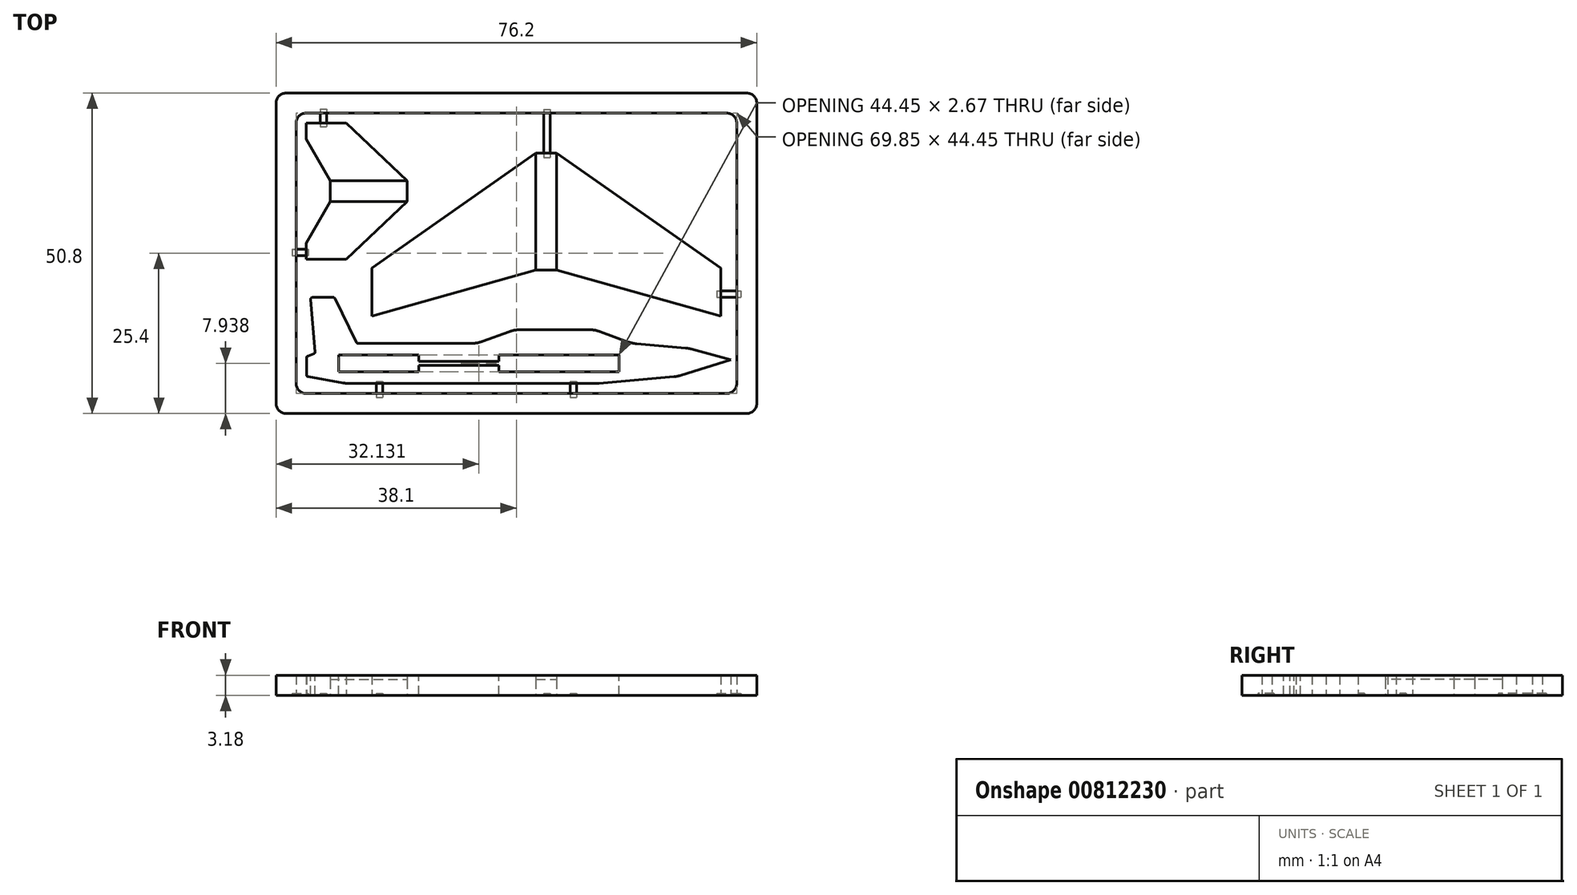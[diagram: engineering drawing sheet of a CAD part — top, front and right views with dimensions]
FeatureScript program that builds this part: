
annotation { "Feature Type Name" : "Feature", "Feature Type Description" : "" }
export const myFeature = defineFeature(function(context is Context, id is Id, definition is map)
    precondition{}
    {
        {
            var Q0;
            Q0=qCreatedBy(makeId("Top.planeOp"),FACE);
            var sketch = newSketch(context, id + "F0", { "sketchPlane" : qUnion([Q0])});
            skLineSegment(sketch, "E0.bottom", {"start": v(1.59, 0) * mm, "end": v(74.61, 0) * mm});
            skLineSegment(sketch, "E0.top", {"start": v(1.59, 50.8) * mm, "end": v(74.61, 50.8) * mm});
            skLineSegment(sketch, "E0.left", {"start": v(0, 1.59) * mm, "end": v(0, 49.21) * mm});
            skLineSegment(sketch, "E0.right", {"start": v(76.2, 1.59) * mm, "end": v(76.2, 49.21) * mm});
            skLineSegment(sketch, "E1.0", {"start": v(73.02, 4.76) * mm, "end": v(73.02, 46.04) * mm});
            skLineSegment(sketch, "E1.1", {"start": v(4.76, 3.17) * mm, "end": v(71.44, 3.17) * mm});
            skLineSegment(sketch, "E1.2", {"start": v(3.17, 4.76) * mm, "end": v(3.17, 46.04) * mm});
            skLineSegment(sketch, "E1.3", {"start": v(4.76, 47.63) * mm, "end": v(71.44, 47.63) * mm});
            skPoint(sketch, "E2.visualSharp", {"position": v(0, 50.8) * mm});
            skArc(sketch, "E2.filletArc", {"start": v(1.59, 50.8) * mm, "mid": v(0.46, 50.34) * mm, "end": v(0, 49.21) * mm});
            skPoint(sketch, "E3.visualSharp", {"position": v(76.2, 50.8) * mm});
            skArc(sketch, "E3.filletArc", {"start": v(76.2, 49.21) * mm, "mid": v(75.74, 50.34) * mm, "end": v(74.61, 50.8) * mm});
            skPoint(sketch, "E4.visualSharp", {"position": v(76.2, 0) * mm});
            skArc(sketch, "E4.filletArc", {"start": v(74.61, 0) * mm, "mid": v(75.74, 0.46) * mm, "end": v(76.2, 1.59) * mm});
            skPoint(sketch, "E5.visualSharp", {"position": v(0, 0) * mm});
            skArc(sketch, "E5.filletArc", {"start": v(0, 1.59) * mm, "mid": v(0.46, 0.46) * mm, "end": v(1.59, 0) * mm});
            skPoint(sketch, "E6.visualSharp", {"position": v(3.17, 3.17) * mm});
            skArc(sketch, "E6.filletArc", {"start": v(3.17, 4.76) * mm, "mid": v(3.64, 3.64) * mm, "end": v(4.76, 3.17) * mm});
            skPoint(sketch, "E7.visualSharp", {"position": v(3.17, 47.63) * mm});
            skArc(sketch, "E7.filletArc", {"start": v(4.76, 47.63) * mm, "mid": v(3.64, 47.16) * mm, "end": v(3.17, 46.04) * mm});
            skPoint(sketch, "E8.visualSharp", {"position": v(73.02, 47.63) * mm});
            skArc(sketch, "E8.filletArc", {"start": v(73.02, 46.04) * mm, "mid": v(72.56, 47.16) * mm, "end": v(71.44, 47.63) * mm});
            skPoint(sketch, "E9.visualSharp", {"position": v(73.02, 3.17) * mm});
            skArc(sketch, "E9.filletArc", {"start": v(71.44, 3.17) * mm, "mid": v(72.56, 3.64) * mm, "end": v(73.02, 4.76) * mm});
            skSolve(sketch);
        }
        {
            var Q0;
            Q0 = qSketchRegion(id + "F0", true);
            extrude(context, id + "F1", {"entities" : qUnion([Q0]), "depth" : 3.17 * mm, "offsetDistance" : 25.4 * mm});
        }
        {
            var Q0;
            Q0=qCreatedBy(makeId("Top.planeOp"),FACE);
            var sketch = newSketch(context, id + "F2", { "sketchPlane" : qUnion([Q0])});
            skLineSegment(sketch, "E10", {"start": v(11.08, 4.76) * mm, "end": v(50.96, 4.76) * mm});
            skLineSegment(sketch, "E11", {"start": v(50.96, 4.76) * mm, "end": v(63.6, 5.87) * mm});
            skLineSegment(sketch, "E12", {"start": v(56.49, 11.11) * mm, "end": v(50.52, 13.28) * mm});
            skLineSegment(sketch, "E13", {"start": v(12.8, 11.11) * mm, "end": v(9.25, 18.4) * mm});
            skLineSegment(sketch, "E14", {"start": v(9.25, 18.4) * mm, "end": v(5.44, 18.4) * mm});
            skLineSegment(sketch, "E15", {"start": v(50.52, 13.28) * mm, "end": v(37.82, 13.28) * mm});
            skLineSegment(sketch, "E16", {"start": v(37.82, 13.28) * mm, "end": v(31.85, 11.11) * mm});
            skLineSegment(sketch, "E17", {"start": v(31.85, 11.11) * mm, "end": v(12.8, 11.11) * mm});
            skLineSegment(sketch, "E18", {"start": v(11.08, 4.76) * mm, "end": v(4.83, 5.87) * mm});
            skLineSegment(sketch, "E19", {"start": v(4.83, 5.87) * mm, "end": v(4.83, 9.04) * mm});
            skLineSegment(sketch, "E20", {"start": v(4.83, 9.04) * mm, "end": v(6.21, 9.55) * mm});
            skLineSegment(sketch, "E21", {"start": v(6.21, 9.55) * mm, "end": v(5.44, 18.4) * mm});
            skLineSegment(sketch, "E22", {"start": v(56.49, 11.11) * mm, "end": v(65.34, 10.34) * mm});
            skLineSegment(sketch, "E23", {"start": v(65.34, 10.34) * mm, "end": v(72.1, 8.53) * mm});
            skLineSegment(sketch, "E24", {"start": v(72.1, 8.53) * mm, "end": v(63.6, 5.87) * mm});
            skSolve(sketch);
        }
        {
            var Q0;
            Q0 = qSketchRegion(id + "F2", true);
            extrude(context, id + "F3", {"entities" : qUnion([Q0]), "depth" : 3.17 * mm, "offsetDistance" : 25.4 * mm});
        }
        {
            var Q0;
            Q0=makeQuery(id+"F3.opExtrude","SWEPT_EDGE",EDGE,{"disambiguationData":[OSD([sQuery(id+"F2.wireOp",EDGE,"E22"),sQuery(id+"F2.wireOp",EDGE,"E23")])]});
            var Q1;
            Q1=makeQuery(id+"F3.opExtrude","SWEPT_EDGE",EDGE,{"disambiguationData":[OSD([sQuery(id+"F2.wireOp",EDGE,"E12"),sQuery(id+"F2.wireOp",EDGE,"E22")])]});
            var Q2;
            Q2=makeQuery(id+"F3.opExtrude","SWEPT_EDGE",EDGE,{"disambiguationData":[OSD([sQuery(id+"F2.wireOp",EDGE,"E12"),sQuery(id+"F2.wireOp",EDGE,"E15")])]});
            var Q3;
            Q3=makeQuery(id+"F3.opExtrude","SWEPT_EDGE",EDGE,{"disambiguationData":[OSD([sQuery(id+"F2.wireOp",EDGE,"E15"),sQuery(id+"F2.wireOp",EDGE,"E16")])]});
            var Q4;
            Q4=makeQuery(id+"F3.opExtrude","SWEPT_EDGE",EDGE,{"disambiguationData":[OSD([sQuery(id+"F2.wireOp",EDGE,"E16"),sQuery(id+"F2.wireOp",EDGE,"E17")])]});
            var Q5;
            Q5=makeQuery(id+"F3.opExtrude","SWEPT_EDGE",EDGE,{"disambiguationData":[OSD([sQuery(id+"F2.wireOp",EDGE,"E11"),sQuery(id+"F2.wireOp",EDGE,"E24")])]});
            var Q6;
            Q6=makeQuery(id+"F3.opExtrude","SWEPT_EDGE",EDGE,{"disambiguationData":[OSD([sQuery(id+"F2.wireOp",EDGE,"E10"),sQuery(id+"F2.wireOp",EDGE,"E11")])]});
            var Q7;
            Q7=makeQuery(id+"F3.opExtrude","SWEPT_EDGE",EDGE,{"disambiguationData":[OSD([sQuery(id+"F2.wireOp",EDGE,"E10"),sQuery(id+"F2.wireOp",EDGE,"E18")])]});
            fillet(context, id + "F4", {"entities" : qUnion([Q0, Q1, Q2, Q3, Q4, Q5, Q6, Q7]), "radius" : 5.08 * mm, "tangentPropagation" : true, "allowEdgeOverflow" : false});
        }
        {
            var Q0;
            Q0=makeQuery(id+"F3.opExtrude","SWEPT_EDGE",EDGE,{"disambiguationData":[OSD([sQuery(id+"F2.wireOp",EDGE,"E18"),sQuery(id+"F2.wireOp",EDGE,"E19")])]});
            var Q1;
            Q1=makeQuery(id+"F3.opExtrude","SWEPT_EDGE",EDGE,{"disambiguationData":[OSD([sQuery(id+"F2.wireOp",EDGE,"E19"),sQuery(id+"F2.wireOp",EDGE,"E20")])]});
            var Q2;
            Q2=makeQuery(id+"F3.opExtrude","SWEPT_EDGE",EDGE,{"disambiguationData":[OSD([sQuery(id+"F2.wireOp",EDGE,"E20"),sQuery(id+"F2.wireOp",EDGE,"E21")])]});
            var Q3;
            Q3=makeQuery(id+"F3.opExtrude","SWEPT_EDGE",EDGE,{"disambiguationData":[OSD([sQuery(id+"F2.wireOp",EDGE,"E14"),sQuery(id+"F2.wireOp",EDGE,"E21")])]});
            var Q4;
            Q4=makeQuery(id+"F3.opExtrude","SWEPT_EDGE",EDGE,{"disambiguationData":[OSD([sQuery(id+"F2.wireOp",EDGE,"E13"),sQuery(id+"F2.wireOp",EDGE,"E14")])]});
            var Q5;
            Q5=makeQuery(id+"F3.opExtrude","SWEPT_EDGE",EDGE,{"disambiguationData":[OSD([sQuery(id+"F2.wireOp",EDGE,"E13"),sQuery(id+"F2.wireOp",EDGE,"E17")])]});
            fillet(context, id + "F5", {"entities" : qUnion([Q0, Q1, Q2, Q3, Q4, Q5]), "radius" : 0.32 * mm, "tangentPropagation" : true, "allowEdgeOverflow" : false});
        }
        {
            var Q0;
            Q0=makeQuery(id+"F3.opExtrude","CAP_FACE",FACE,{"disambiguationData":[OSD([sQuery(id+"F2.wireOp",EDGE,"E10"),sQuery(id+"F2.wireOp",EDGE,"E11"),sQuery(id+"F2.wireOp",EDGE,"E12"),sQuery(id+"F2.wireOp",EDGE,"E13"),sQuery(id+"F2.wireOp",EDGE,"E14"),sQuery(id+"F2.wireOp",EDGE,"E15"),sQuery(id+"F2.wireOp",EDGE,"E16"),sQuery(id+"F2.wireOp",EDGE,"E17"),sQuery(id+"F2.wireOp",EDGE,"E18"),sQuery(id+"F2.wireOp",EDGE,"E19"),sQuery(id+"F2.wireOp",EDGE,"E20"),sQuery(id+"F2.wireOp",EDGE,"E21"),sQuery(id+"F2.wireOp",EDGE,"E22"),sQuery(id+"F2.wireOp",EDGE,"E23"),sQuery(id+"F2.wireOp",EDGE,"E24")])],"isStart":false});
            var sketch = newSketch(context, id + "F6", { "sketchPlane" : qUnion([Q0])});
            skLineSegment(sketch, "E25.bottom", {"start": v(9.9, 9.27) * mm, "end": v(22.6, 9.27) * mm});
            skLineSegment(sketch, "E25.top", {"start": v(9.9, 6.6) * mm, "end": v(22.6, 6.6) * mm});
            skLineSegment(sketch, "E25.left", {"start": v(9.9, 9.27) * mm, "end": v(9.9, 6.6) * mm});
            skLineSegment(sketch, "E25.right", {"start": v(22.6, 9.27) * mm, "end": v(22.6, 8.25) * mm});
            skLineSegment(sketch, "E26.bottom", {"start": v(35.3, 9.27) * mm, "end": v(54.36, 9.27) * mm});
            skLineSegment(sketch, "E26.top", {"start": v(35.3, 6.6) * mm, "end": v(54.36, 6.6) * mm});
            skLineSegment(sketch, "E26.left", {"start": v(35.3, 9.27) * mm, "end": v(35.3, 8.25) * mm});
            skLineSegment(sketch, "E26.right", {"start": v(54.36, 9.27) * mm, "end": v(54.36, 6.6) * mm});
            skLineSegment(sketch, "E27", {"start": v(22.6, 9.27) * mm, "end": v(22.6, 11.11) * mm, "construction": true});
            skLineSegment(sketch, "E28", {"start": v(22.6, 6.6) * mm, "end": v(22.6, 4.76) * mm, "construction": true});
            skLineSegment(sketch, "E29.bottom", {"start": v(22.6, 8.25) * mm, "end": v(35.3, 8.25) * mm});
            skLineSegment(sketch, "E29.top", {"start": v(22.6, 7.62) * mm, "end": v(35.3, 7.62) * mm});
            skLineSegment(sketch, "E30.trimOffspring", {"start": v(22.6, 7.62) * mm, "end": v(22.6, 6.6) * mm});
            skLineSegment(sketch, "E31.trimOffspring", {"start": v(35.3, 7.62) * mm, "end": v(35.3, 6.6) * mm});
            skSolve(sketch);
        }
        {
            var Q0;
            Q0 = qSketchRegion(id + "F6", true);
            extrude(context, id + "F7", {"entities" : qUnion([Q0]), "operationType" : NewBodyOperationType.REMOVE, "oppositeDirection" : true, "depth" : 25.4 * mm, "offsetDistance" : 25.4 * mm});
        }
        {
            var Q0;
            Q0=qCreatedBy(makeId("Top.planeOp"),FACE);
            var sketch = newSketch(context, id + "F8", { "sketchPlane" : qUnion([Q0])});
            skLineSegment(sketch, "E32.bottom", {"start": v(8.57, 36.9) * mm, "end": v(20.76, 36.9) * mm});
            skLineSegment(sketch, "E32.top", {"start": v(8.57, 33.6) * mm, "end": v(20.76, 33.6) * mm});
            skLineSegment(sketch, "E32.left", {"start": v(8.57, 36.9) * mm, "end": v(8.57, 33.6) * mm});
            skLineSegment(sketch, "E32.right", {"start": v(20.76, 36.9) * mm, "end": v(20.76, 33.6) * mm});
            skLineSegment(sketch, "E33", {"start": v(8.57, 36.9) * mm, "end": v(4.76, 43.5) * mm});
            skLineSegment(sketch, "E34", {"start": v(4.76, 43.5) * mm, "end": v(4.76, 46.04) * mm});
            skLineSegment(sketch, "E35", {"start": v(4.76, 46.04) * mm, "end": v(11.11, 46.04) * mm});
            skLineSegment(sketch, "E36", {"start": v(11.11, 46.04) * mm, "end": v(20.76, 36.9) * mm});
            skLineSegment(sketch, "E37", {"start": v(8.57, 33.6) * mm, "end": v(4.76, 27) * mm});
            skLineSegment(sketch, "E38", {"start": v(4.76, 27) * mm, "end": v(4.76, 24.46) * mm});
            skLineSegment(sketch, "E39", {"start": v(4.76, 24.46) * mm, "end": v(11.11, 24.46) * mm});
            skLineSegment(sketch, "E40", {"start": v(11.11, 24.46) * mm, "end": v(20.76, 33.6) * mm});
            skSolve(sketch);
        }
        {
            var Q0;
            Q0 = qSketchRegion(id + "F8", true);
            extrude(context, id + "F9", {"entities" : qUnion([Q0]), "depth" : 3.17 * mm, "offsetDistance" : 25.4 * mm});
        }
        {
            var Q0;
            Q0=makeQuery(id+"F9.opExtrude","CAP_FACE",FACE,{"disambiguationData":[OSD([sQuery(id+"F8.wireOp",EDGE,"E32.left"),sQuery(id+"F8.wireOp",EDGE,"E32.right"),sQuery(id+"F8.wireOp",EDGE,"E33"),sQuery(id+"F8.wireOp",EDGE,"E34"),sQuery(id+"F8.wireOp",EDGE,"E35"),sQuery(id+"F8.wireOp",EDGE,"E36"),sQuery(id+"F8.wireOp",EDGE,"E37"),sQuery(id+"F8.wireOp",EDGE,"E38"),sQuery(id+"F8.wireOp",EDGE,"E39"),sQuery(id+"F8.wireOp",EDGE,"E40")])],"isStart":false});
            var sketch = newSketch(context, id + "F10", { "sketchPlane" : qUnion([Q0])});
            skLineSegment(sketch, "E41.bottom", {"start": v(8.57, 36.9) * mm, "end": v(20.76, 36.9) * mm});
            skLineSegment(sketch, "E41.top", {"start": v(8.57, 33.6) * mm, "end": v(20.76, 33.6) * mm});
            skLineSegment(sketch, "E41.left", {"start": v(8.57, 36.9) * mm, "end": v(8.57, 33.6) * mm});
            skLineSegment(sketch, "E41.right", {"start": v(20.76, 36.9) * mm, "end": v(20.76, 33.6) * mm});
            skSolve(sketch);
        }
        {
            var Q0;
            Q0 = qSketchRegion(id + "F10", true);
            extrude(context, id + "F11", {"entities" : qUnion([Q0]), "operationType" : NewBodyOperationType.REMOVE, "oppositeDirection" : true, "depth" : 0.66 * mm, "offsetDistance" : 25.4 * mm});
        }
        {
            var Q0;
            Q0=qCreatedBy(makeId("Top.planeOp"),FACE);
            var sketch = newSketch(context, id + "F12", { "sketchPlane" : qUnion([Q0])});
            skLineSegment(sketch, "E42.bottom", {"start": v(41.17, 41.28) * mm, "end": v(44.48, 41.28) * mm});
            skLineSegment(sketch, "E42.top", {"start": v(41.17, 22.73) * mm, "end": v(44.48, 22.73) * mm});
            skLineSegment(sketch, "E42.left", {"start": v(41.17, 41.28) * mm, "end": v(41.17, 22.73) * mm});
            skLineSegment(sketch, "E42.right", {"start": v(44.48, 41.28) * mm, "end": v(44.48, 22.73) * mm});
            skLineSegment(sketch, "E43", {"start": v(41.17, 41.28) * mm, "end": v(15.17, 23.06) * mm});
            skLineSegment(sketch, "E44", {"start": v(15.17, 23.06) * mm, "end": v(15.17, 15.44) * mm});
            skLineSegment(sketch, "E45", {"start": v(15.17, 15.44) * mm, "end": v(41.17, 22.73) * mm});
            skLineSegment(sketch, "E46", {"start": v(44.48, 41.28) * mm, "end": v(70.48, 23.06) * mm});
            skLineSegment(sketch, "E47", {"start": v(70.48, 23.06) * mm, "end": v(70.48, 15.44) * mm});
            skLineSegment(sketch, "E48", {"start": v(70.48, 15.44) * mm, "end": v(44.48, 22.73) * mm});
            skSolve(sketch);
        }
        {
            var Q0;
            Q0 = qSketchRegion(id + "F12", true);
            extrude(context, id + "F13", {"entities" : qUnion([Q0]), "depth" : 3.17 * mm, "offsetDistance" : 25.4 * mm});
        }
        {
            var Q0;
            Q0=makeQuery(id+"F13.opExtrude","CAP_FACE",FACE,{"disambiguationData":[OSD([sQuery(id+"F12.wireOp",EDGE,"E42.bottom"),sQuery(id+"F12.wireOp",EDGE,"E42.top"),sQuery(id+"F12.wireOp",EDGE,"E43"),sQuery(id+"F12.wireOp",EDGE,"E44"),sQuery(id+"F12.wireOp",EDGE,"E45"),sQuery(id+"F12.wireOp",EDGE,"E46"),sQuery(id+"F12.wireOp",EDGE,"E47"),sQuery(id+"F12.wireOp",EDGE,"E48")])],"isStart":false});
            var sketch = newSketch(context, id + "F14", { "sketchPlane" : qUnion([Q0])});
            skLineSegment(sketch, "E49.bottom", {"start": v(41.17, 41.28) * mm, "end": v(44.48, 41.28) * mm});
            skLineSegment(sketch, "E49.top", {"start": v(41.17, 22.73) * mm, "end": v(44.48, 22.73) * mm});
            skLineSegment(sketch, "E49.left", {"start": v(41.17, 41.28) * mm, "end": v(41.17, 22.73) * mm});
            skLineSegment(sketch, "E49.right", {"start": v(44.48, 41.28) * mm, "end": v(44.48, 22.73) * mm});
            skSolve(sketch);
        }
        {
            var Q0;
            Q0 = qSketchRegion(id + "F14", true);
            extrude(context, id + "F15", {"entities" : qUnion([Q0]), "operationType" : NewBodyOperationType.REMOVE, "oppositeDirection" : true, "depth" : 0.66 * mm, "offsetDistance" : 25.4 * mm});
        }
        {
            var Q0;
            Q0=qCreatedBy(makeId("Top.planeOp"),FACE);
            var sketch = newSketch(context, id + "F16", { "sketchPlane" : qUnion([Q0])});
            skLineSegment(sketch, "E50.bottom", {"start": v(69.85, 19.43) * mm, "end": v(73.66, 19.43) * mm});
            skLineSegment(sketch, "E50.top", {"start": v(69.85, 18.41) * mm, "end": v(73.66, 18.41) * mm});
            skLineSegment(sketch, "E50.left", {"start": v(69.85, 19.43) * mm, "end": v(69.85, 18.41) * mm});
            skLineSegment(sketch, "E50.right", {"start": v(73.66, 19.43) * mm, "end": v(73.66, 18.41) * mm});
            skLineSegment(sketch, "E51.bottom", {"start": v(42.41, 48.22) * mm, "end": v(43.43, 48.22) * mm});
            skLineSegment(sketch, "E51.top", {"start": v(42.41, 40.6) * mm, "end": v(43.43, 40.6) * mm});
            skLineSegment(sketch, "E51.left", {"start": v(42.41, 48.22) * mm, "end": v(42.41, 40.6) * mm});
            skLineSegment(sketch, "E51.right", {"start": v(43.43, 48.22) * mm, "end": v(43.43, 40.6) * mm});
            skLineSegment(sketch, "E52.bottom", {"start": v(46.6, 5.08) * mm, "end": v(47.62, 5.08) * mm});
            skLineSegment(sketch, "E52.top", {"start": v(46.6, 2.54) * mm, "end": v(47.62, 2.54) * mm});
            skLineSegment(sketch, "E52.left", {"start": v(46.6, 5.08) * mm, "end": v(46.6, 2.54) * mm});
            skLineSegment(sketch, "E52.right", {"start": v(47.62, 5.08) * mm, "end": v(47.62, 2.54) * mm});
            skLineSegment(sketch, "E53.bottom", {"start": v(15.87, 5.08) * mm, "end": v(16.9, 5.08) * mm});
            skLineSegment(sketch, "E53.top", {"start": v(15.87, 2.54) * mm, "end": v(16.9, 2.54) * mm});
            skLineSegment(sketch, "E53.left", {"start": v(15.87, 5.08) * mm, "end": v(15.87, 2.54) * mm});
            skLineSegment(sketch, "E53.right", {"start": v(16.9, 5.08) * mm, "end": v(16.9, 2.54) * mm});
            skLineSegment(sketch, "E54.bottom", {"start": v(2.54, 26.04) * mm, "end": v(5.08, 26.04) * mm});
            skLineSegment(sketch, "E54.top", {"start": v(2.54, 25.02) * mm, "end": v(5.08, 25.02) * mm});
            skLineSegment(sketch, "E54.left", {"start": v(2.54, 26.04) * mm, "end": v(2.54, 25.02) * mm});
            skLineSegment(sketch, "E54.right", {"start": v(5.08, 26.04) * mm, "end": v(5.08, 25.02) * mm});
            skLineSegment(sketch, "E55.bottom", {"start": v(6.98, 48.26) * mm, "end": v(8, 48.26) * mm});
            skLineSegment(sketch, "E55.top", {"start": v(6.98, 45.47) * mm, "end": v(8, 45.47) * mm});
            skLineSegment(sketch, "E55.left", {"start": v(6.98, 48.26) * mm, "end": v(6.98, 45.47) * mm});
            skLineSegment(sketch, "E55.right", {"start": v(8, 48.26) * mm, "end": v(8, 45.47) * mm});
            skSolve(sketch);
        }
        {
            var Q0;
            Q0 = qSketchRegion(id + "F16", true);
            extrude(context, id + "F17", {"entities" : qUnion([Q0]), "depth" : 0.32 * mm, "offsetDistance" : 25.4 * mm});
        }
    });
